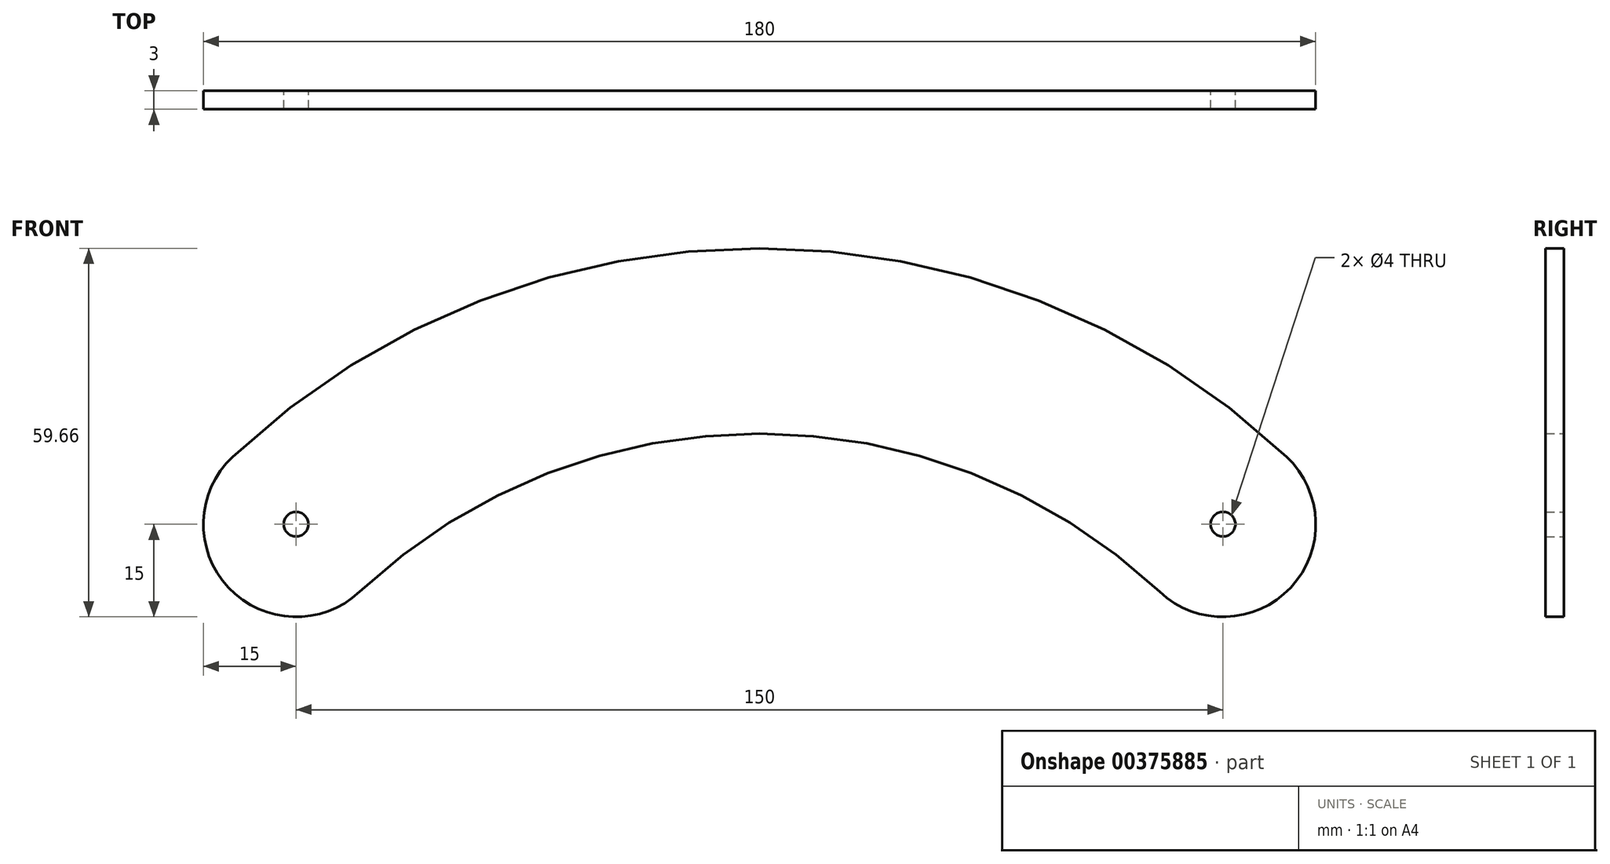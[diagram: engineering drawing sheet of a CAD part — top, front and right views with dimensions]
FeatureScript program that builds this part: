
annotation { "Feature Type Name" : "Feature", "Feature Type Description" : "" }
export const myFeature = defineFeature(function(context is Context, id is Id, definition is map)
    precondition{}
    {
        {
            assignVariable(context, id + "F0", {"name" : "Tykkelse", "anyValue" : 3});
        }
        {
            var Q0;
            Q0=qCreatedBy(makeId("Front.planeOp"),FACE);
            var sketch = newSketch(context, id + "F1", { "sketchPlane" : qUnion([Q0])});
            skArc(sketch, "E0", {"start": v(64.74, -10.94) * mm, "mid": v(85.94, -10.26) * mm, "end": v(85.26, 10.94) * mm});
            skArc(sketch, "E1.MirrorC", {"start": v(-64.74, -10.94) * mm, "mid": v(-85.94, -10.26) * mm, "end": v(-85.26, 10.94) * mm});
            skArc(sketch, "E2", {"start": v(85.26, 10.94) * mm, "mid": v(0, 44.66) * mm, "end": v(-85.26, 10.94) * mm});
            skArc(sketch, "E3", {"start": v(64.74, -10.94) * mm, "mid": v(0, 14.66) * mm, "end": v(-64.74, -10.94) * mm});
            skCircle(sketch, "E4", {"center": v(75, 0) * mm, "radius": 2 * mm});
            skCircle(sketch, "E5.MirrorC", {"center": v(-75, 0) * mm, "radius": 2 * mm});
            skSolve(sketch);
        }
        {
            var Q0;
            Q0 = qSketchRegion(id + "F1", true);
            extrude(context, id + "F2", {"entities" : qUnion([Q0]), "depth" : (getVariable(context, 'Tykkelse')) * mm, "symmetric" : true});
        }
    });
